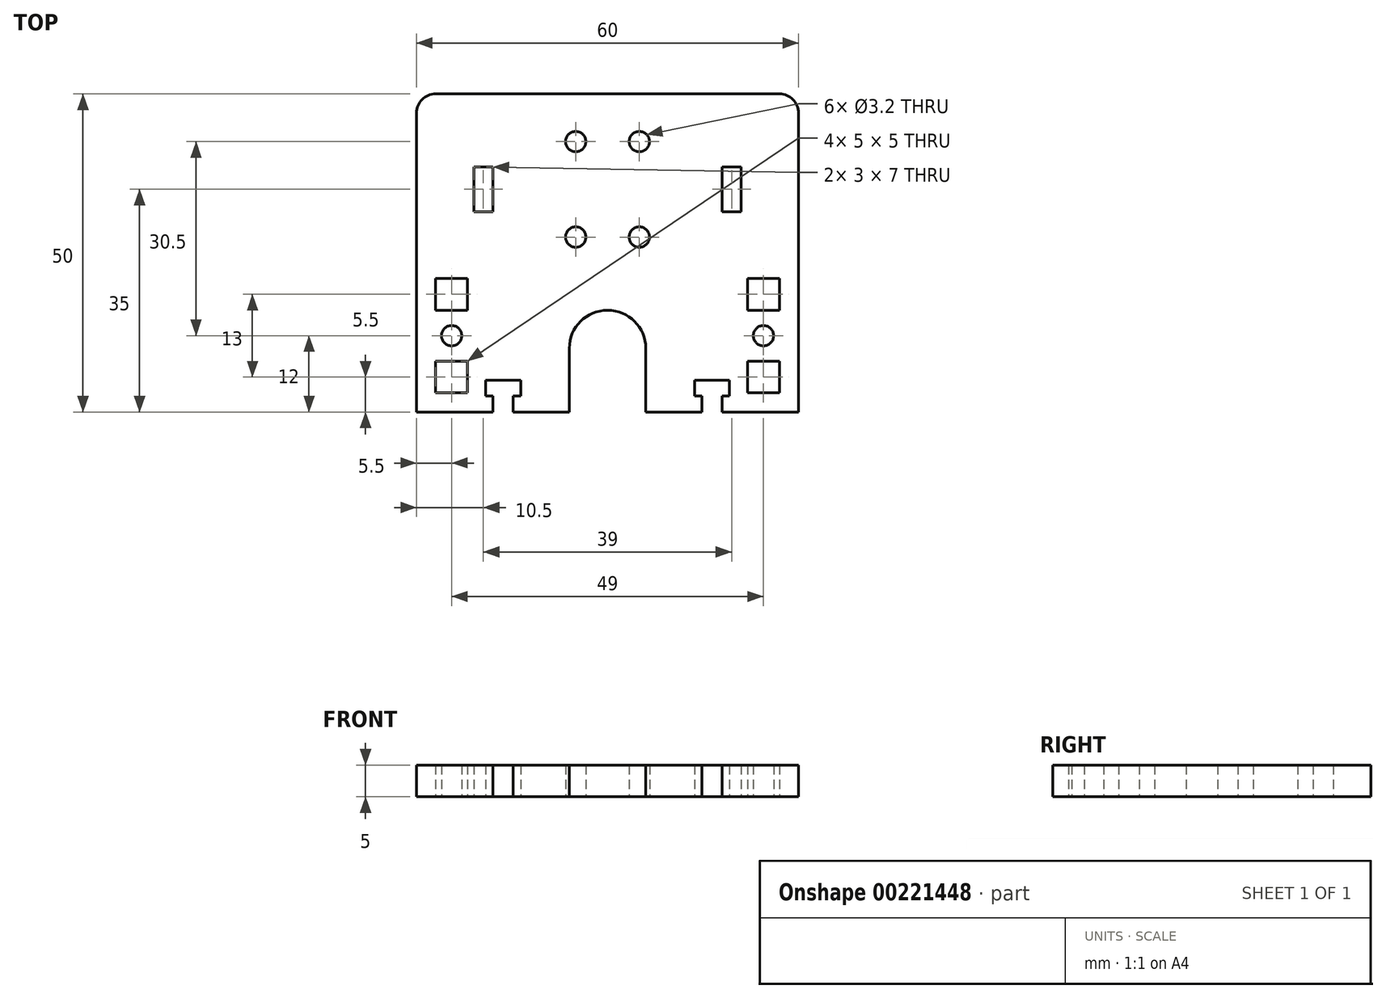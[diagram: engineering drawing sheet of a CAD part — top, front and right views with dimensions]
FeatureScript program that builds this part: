
annotation { "Feature Type Name" : "Feature", "Feature Type Description" : "" }
export const myFeature = defineFeature(function(context is Context, id is Id, definition is map)
    precondition{}
    {
        {
            assignVariable(context, id + "F0", {"name" : "thickness", "anyValue" : 5 * mm});
        }
        {
            var Q0;
            Q0=qCreatedBy(makeId("Top.planeOp"),FACE);
            var sketch = newSketch(context, id + "F1", { "sketchPlane" : qUnion([Q0])});
            skLineSegment(sketch, "E0.bottom", {"start": v(15, 10) * mm, "end": v(-15, 10) * mm, "construction": true});
            skLineSegment(sketch, "E0.top", {"start": v(15, -10) * mm, "end": v(-15, -10) * mm, "construction": true});
            skLineSegment(sketch, "E0.left", {"start": v(15, 10) * mm, "end": v(15, -10) * mm, "construction": true});
            skLineSegment(sketch, "E0.right", {"start": v(-15, 10) * mm, "end": v(-15, -10) * mm, "construction": true});
            skPoint(sketch, "E0.middle", {"position": v(0, 0) * mm});
            skLineSegment(sketch, "E1", {"start": v(-15, 0) * mm, "end": v(15, 0) * mm, "construction": true});
            skLineSegment(sketch, "E2", {"start": v(0, 10) * mm, "end": v(0, -10) * mm, "construction": true});
            skCircle(sketch, "E3", {"center": v(-5, -7.5) * mm, "radius": 1.6 * mm});
            skCircle(sketch, "E4", {"center": v(5, -7.5) * mm, "radius": 1.6 * mm});
            skCircle(sketch, "E5", {"center": v(5, 7.5) * mm, "radius": 1.6 * mm});
            skCircle(sketch, "E6", {"center": v(-5, 7.5) * mm, "radius": 1.6 * mm});
            skLineSegment(sketch, "E7", {"start": v(-5, 7.5) * mm, "end": v(5, 7.5) * mm, "construction": true});
            skLineSegment(sketch, "E8", {"start": v(5, -7.5) * mm, "end": v(5, 7.5) * mm, "construction": true});
            skPoint(sketch, "E9", {"position": v(5, 0) * mm});
            skPoint(sketch, "E10", {"position": v(0, 7.5) * mm});
            skLineSegment(sketch, "E11.top", {"start": v(27, 15) * mm, "end": v(-27, 15) * mm});
            skArc(sketch, "E12", {"start": v(6, -25) * mm, "mid": v(0, -19) * mm, "end": v(-6, -25) * mm});
            skArc(sketch, "E13", {"start": v(6, -25) * mm, "mid": v(0, -31) * mm, "end": v(-6, -25) * mm, "construction": true});
            skLineSegment(sketch, "E14", {"start": v(-6, -25) * mm, "end": v(-6, -35) * mm});
            skLineSegment(sketch, "E15", {"start": v(-6, -35) * mm, "end": v(-14.8, -35) * mm});
            skPoint(sketch, "E16.visualSharp", {"position": v(-6, -35) * mm});
            skLineSegment(sketch, "E17", {"start": v(-30, 12) * mm, "end": v(-30, -35) * mm});
            skLineSegment(sketch, "E18", {"start": v(30, 12) * mm, "end": v(30, -35) * mm});
            skLineSegment(sketch, "E19", {"start": v(30, -35) * mm, "end": v(18, -35) * mm});
            skPoint(sketch, "E20.visualSharp", {"position": v(6, -35) * mm});
            skLineSegment(sketch, "E21.bottom", {"start": v(-21, 3.5) * mm, "end": v(-18, 3.5) * mm});
            skLineSegment(sketch, "E21.top", {"start": v(-21, -3.5) * mm, "end": v(-18, -3.5) * mm});
            skLineSegment(sketch, "E21.left", {"start": v(-21, 3.5) * mm, "end": v(-21, -3.5) * mm});
            skLineSegment(sketch, "E21.right", {"start": v(-18, 3.5) * mm, "end": v(-18, -3.5) * mm});
            skPoint(sketch, "E22", {"position": v(-18, 0) * mm});
            skLineSegment(sketch, "E23.MirrorCS", {"start": v(21, 3.5) * mm, "end": v(18, 3.5) * mm});
            skLineSegment(sketch, "E24.MirrorCS", {"start": v(21, 3.5) * mm, "end": v(21, -3.5) * mm});
            skLineSegment(sketch, "E25.MirrorCS", {"start": v(21, -3.5) * mm, "end": v(18, -3.5) * mm});
            skLineSegment(sketch, "E26.MirrorCS", {"start": v(18, 3.5) * mm, "end": v(18, -3.5) * mm});
            skPoint(sketch, "E27.MirrorP", {"position": v(18, 0) * mm});
            skLineSegment(sketch, "E28.bottom", {"start": v(-27, -32) * mm, "end": v(-22, -32) * mm});
            skLineSegment(sketch, "E28.top", {"start": v(-27, -27) * mm, "end": v(-22, -27) * mm});
            skLineSegment(sketch, "E28.left", {"start": v(-27, -32) * mm, "end": v(-27, -27) * mm});
            skLineSegment(sketch, "E28.right", {"start": v(-22, -32) * mm, "end": v(-22, -27) * mm});
            skPoint(sketch, "E29.firstSnap0", {"position": v(-27, -29.5) * mm});
            skLineSegment(sketch, "E29.bottom", {"start": v(-27, -19) * mm, "end": v(-22, -19) * mm});
            skLineSegment(sketch, "E29.top", {"start": v(-27, -14) * mm, "end": v(-22, -14) * mm});
            skLineSegment(sketch, "E29.left", {"start": v(-27, -19) * mm, "end": v(-27, -14) * mm});
            skLineSegment(sketch, "E29.right", {"start": v(-22, -19) * mm, "end": v(-22, -14) * mm});
            skCircle(sketch, "E30", {"center": v(-24.5, -23) * mm, "radius": 1.6 * mm});
            skPoint(sketch, "E30.centerSnap0", {"position": v(-24.5, -19) * mm});
            skLineSegment(sketch, "E31.MirrorCS", {"start": v(22, -32) * mm, "end": v(22, -27) * mm});
            skLineSegment(sketch, "E32.MirrorCS", {"start": v(27, -32) * mm, "end": v(22, -32) * mm});
            skLineSegment(sketch, "E33.MirrorCS", {"start": v(22, -19) * mm, "end": v(22, -14) * mm});
            skLineSegment(sketch, "E34.MirrorCS", {"start": v(27, -19) * mm, "end": v(22, -19) * mm});
            skPoint(sketch, "E35.MirrorP", {"position": v(27, -29.5) * mm});
            skLineSegment(sketch, "E36.MirrorCS", {"start": v(27, -32) * mm, "end": v(27, -27) * mm});
            skPoint(sketch, "E37.MirrorP", {"position": v(24.5, -19) * mm});
            skLineSegment(sketch, "E38.MirrorCS", {"start": v(27, -14) * mm, "end": v(22, -14) * mm});
            skLineSegment(sketch, "E39.MirrorCS", {"start": v(27, -19) * mm, "end": v(27, -14) * mm});
            skLineSegment(sketch, "E40.MirrorCS", {"start": v(27, -27) * mm, "end": v(22, -27) * mm});
            skCircle(sketch, "E41.MirrorC", {"center": v(24.5, -23) * mm, "radius": 1.6 * mm});
            skPoint(sketch, "E42.visualSharp", {"position": v(-30, -35) * mm});
            skPoint(sketch, "E43.visualSharp", {"position": v(30, -35) * mm});
            skPoint(sketch, "E44.visualSharp", {"position": v(30, 15) * mm});
            skArc(sketch, "E44.filletArc", {"start": v(30, 12) * mm, "mid": v(29.12, 14.12) * mm, "end": v(27, 15) * mm});
            skPoint(sketch, "E45.visualSharp", {"position": v(-30, 15) * mm});
            skArc(sketch, "E45.filletArc", {"start": v(-27, 15) * mm, "mid": v(-29.12, 14.12) * mm, "end": v(-30, 12) * mm});
            skLineSegment(sketch, "E46.trimOffspring", {"start": v(6, -35) * mm, "end": v(6, -25) * mm});
            skLineSegment(sketch, "E47", {"start": v(-18, -35) * mm, "end": v(-18, -32.5) * mm});
            skLineSegment(sketch, "E48", {"start": v(-18, -32.5) * mm, "end": v(-19.15, -32.5) * mm});
            skLineSegment(sketch, "E49", {"start": v(-19.15, -32.5) * mm, "end": v(-19.15, -30) * mm});
            skLineSegment(sketch, "E50", {"start": v(-19.15, -30) * mm, "end": v(-16.4, -30) * mm});
            skLineSegment(sketch, "E51", {"start": v(-16.4, -30) * mm, "end": v(-16.4, -35) * mm, "construction": true});
            skLineSegment(sketch, "E52.MirrorCS", {"start": v(-13.65, -30) * mm, "end": v(-16.4, -30) * mm});
            skLineSegment(sketch, "E53.MirrorCS", {"start": v(-13.65, -32.5) * mm, "end": v(-13.65, -30) * mm});
            skLineSegment(sketch, "E54.MirrorCS", {"start": v(-14.8, -32.5) * mm, "end": v(-13.65, -32.5) * mm});
            skLineSegment(sketch, "E55.MirrorCS", {"start": v(-14.8, -35) * mm, "end": v(-14.8, -32.5) * mm});
            skLineSegment(sketch, "E56.MirrorCS", {"start": v(14.8, -32.5) * mm, "end": v(13.65, -32.5) * mm});
            skLineSegment(sketch, "E57.MirrorCS", {"start": v(18, -32.5) * mm, "end": v(19.15, -32.5) * mm});
            skLineSegment(sketch, "E58.MirrorCS", {"start": v(14.8, -35) * mm, "end": v(14.8, -32.5) * mm});
            skLineSegment(sketch, "E59.MirrorCS", {"start": v(19.15, -32.5) * mm, "end": v(19.15, -30) * mm});
            skLineSegment(sketch, "E60.MirrorCS", {"start": v(19.15, -30) * mm, "end": v(16.4, -30) * mm});
            skLineSegment(sketch, "E61.MirrorCS", {"start": v(18, -35) * mm, "end": v(18, -32.5) * mm});
            skLineSegment(sketch, "E62.MirrorCS", {"start": v(13.65, -30) * mm, "end": v(16.4, -30) * mm});
            skLineSegment(sketch, "E63.MirrorCS", {"start": v(16.4, -30) * mm, "end": v(16.4, -35) * mm, "construction": true});
            skLineSegment(sketch, "E64.MirrorCS", {"start": v(13.65, -32.5) * mm, "end": v(13.65, -30) * mm});
            skLineSegment(sketch, "E65.trimOffspring", {"start": v(-18, -35) * mm, "end": v(-30, -35) * mm});
            skLineSegment(sketch, "E66.trimOffspring", {"start": v(14.8, -35) * mm, "end": v(6, -35) * mm});
            skSolve(sketch);
        }
        {
            var Q0;
            Q0 = qSketchRegion(id + "F1", true);
            extrude(context, id + "F2", {"entities" : qUnion([Q0]), "depth" : getVariable(context, 'thickness')});
        }
    });
